# Revit family: KF4.213
name_source: partatom
category: Plumbing Fixtures
revit_build: Autodesk Revit Architecture 2012 (Build: 20110309_2315(x64)
units: mm (PartAtom-declared; Revit-internal decimal feet)

## types (1)
- KF4.213
    Assembly Code = D2010
    CW Connection = Yes
    CWFU = 0
    Cost = 0 $
    Default Elevation = 0' - 0"
    Description = Junior econo flush, front access box. Back entry with flush pipes.
    Elbow connector = C-FM8.45
    Flushpipe = FJT1.2 and FMT3.4
    HW Connection = No
    HWFU = 0
    Keynote = For high pressure installations
    Manufacturer = COBRA
    Material = Chrome - Brushed
    Model = KF4.213
    Palm pushbutton assembly = C-KM9.16
    Piston assembly = C-FJ8.10
    Pushbutton assembly = C-FJ8.20
    Range = Junior Flushmaster Flushvalves
    Rubber pan connector = C-FM8.3
    Top cover = C-FJC1.2
    Type Comments = SANS 1240
    URL = http://www.cobra.co.za
    Vent Connection = No
    WFU = 0
    Waste Connection = No

## geometry (parser evidence)
native form markers: Blend x7
no freeform markers — native parametric forms only
